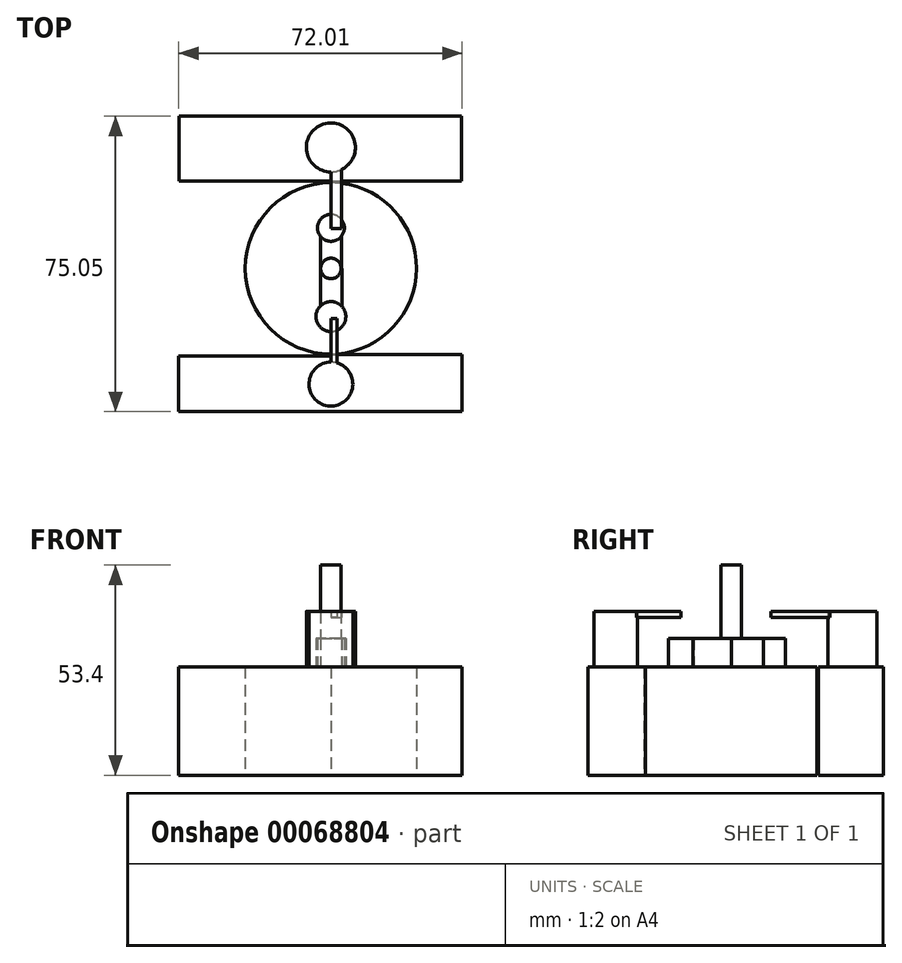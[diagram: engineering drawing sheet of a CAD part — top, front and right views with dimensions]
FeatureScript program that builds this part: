
annotation { "Feature Type Name" : "Feature", "Feature Type Description" : "" }
export const myFeature = defineFeature(function(context is Context, id is Id, definition is map)
    precondition{}
    {
        {
            var Q0;
            Q0=qCreatedBy(makeId("Top.planeOp"),FACE);
            var sketch = newSketch(context, id + "F0", { "sketchPlane" : qUnion([Q0])});
            skCircle(sketch, "E0", {"center": v(0, 0) * mm, "radius": 21.76 * mm});
            skLineSegment(sketch, "E1", {"start": v(0, 0) * mm, "end": v(0, 38.66) * mm});
            skLineSegment(sketch, "E2", {"start": v(0, 38.66) * mm, "end": v(0, 0) * mm});
            skLineSegment(sketch, "E3", {"start": v(0, 0) * mm, "end": v(33.39, 0) * mm});
            skLineSegment(sketch, "E4", {"start": v(33.39, 0) * mm, "end": v(-32.47, 0) * mm});
            skLineSegment(sketch, "E5", {"start": v(-32.47, 0) * mm, "end": v(0, 0) * mm});
            skLineSegment(sketch, "E6", {"start": v(0, -36.39) * mm, "end": v(0, 0) * mm});
            skLineSegment(sketch, "E7.bottom", {"start": v(0, 38.66) * mm, "end": v(-38.56, 38.66) * mm});
            skLineSegment(sketch, "E7.top", {"start": v(0, 22.23) * mm, "end": v(-38.56, 22.23) * mm});
            skLineSegment(sketch, "E7.left", {"start": v(0, 38.66) * mm, "end": v(0, 22.23) * mm});
            skLineSegment(sketch, "E7.right", {"start": v(-38.56, 38.66) * mm, "end": v(-38.56, 22.23) * mm});
            skLineSegment(sketch, "E8.bottom", {"start": v(-38.56, 22.23) * mm, "end": v(-32.47, 22.23) * mm});
            skLineSegment(sketch, "E8.top", {"start": v(-38.56, 0) * mm, "end": v(-32.47, 0) * mm});
            skLineSegment(sketch, "E8.left", {"start": v(-38.56, 22.23) * mm, "end": v(-38.56, 0) * mm});
            skLineSegment(sketch, "E8.right", {"start": v(-32.47, 22.23) * mm, "end": v(-32.47, 0) * mm});
            skLineSegment(sketch, "E9.bottom", {"start": v(0, -36.39) * mm, "end": v(-38.67, -36.39) * mm});
            skLineSegment(sketch, "E9.top", {"start": v(0, -22.24) * mm, "end": v(-38.67, -22.24) * mm});
            skLineSegment(sketch, "E9.left", {"start": v(0, -36.39) * mm, "end": v(0, -22.24) * mm});
            skLineSegment(sketch, "E9.right", {"start": v(-38.67, -36.39) * mm, "end": v(-38.67, -22.24) * mm});
            skLineSegment(sketch, "E10.bottom", {"start": v(-38.56, 0) * mm, "end": v(-32.87, 0) * mm});
            skLineSegment(sketch, "E10.top", {"start": v(-38.56, -22.24) * mm, "end": v(-32.87, -22.24) * mm});
            skLineSegment(sketch, "E10.left", {"start": v(-38.56, 0) * mm, "end": v(-38.56, -22.24) * mm});
            skLineSegment(sketch, "E10.right", {"start": v(-32.87, 0) * mm, "end": v(-32.87, -22.24) * mm});
            skLineSegment(sketch, "E11.bottom", {"start": v(0, 38.66) * mm, "end": v(33.24, 38.66) * mm});
            skLineSegment(sketch, "E11.top", {"start": v(0, 22.13) * mm, "end": v(33.24, 22.13) * mm});
            skLineSegment(sketch, "E11.left", {"start": v(0, 38.66) * mm, "end": v(0, 22.13) * mm});
            skLineSegment(sketch, "E11.right", {"start": v(33.24, 38.66) * mm, "end": v(33.24, 22.13) * mm});
            skLineSegment(sketch, "E12.bottom", {"start": v(33.39, 0) * mm, "end": v(27.74, 0) * mm});
            skLineSegment(sketch, "E12.top", {"start": v(33.39, 22.13) * mm, "end": v(27.74, 22.13) * mm});
            skLineSegment(sketch, "E12.left", {"start": v(33.39, 0) * mm, "end": v(33.39, 22.13) * mm});
            skLineSegment(sketch, "E12.right", {"start": v(27.74, 0) * mm, "end": v(27.74, 22.13) * mm});
            skLineSegment(sketch, "E13.bottom", {"start": v(0, -36.39) * mm, "end": v(33.34, -36.39) * mm});
            skLineSegment(sketch, "E13.top", {"start": v(0, -21.86) * mm, "end": v(33.34, -21.86) * mm});
            skLineSegment(sketch, "E13.left", {"start": v(0, -36.39) * mm, "end": v(0, -21.86) * mm});
            skLineSegment(sketch, "E13.right", {"start": v(33.34, -36.39) * mm, "end": v(33.34, -21.86) * mm});
            skLineSegment(sketch, "E14.bottom", {"start": v(33.34, -21.86) * mm, "end": v(27.74, -21.86) * mm});
            skLineSegment(sketch, "E14.top", {"start": v(33.34, 0) * mm, "end": v(27.74, 0) * mm});
            skLineSegment(sketch, "E14.left", {"start": v(33.34, -21.86) * mm, "end": v(33.34, 0) * mm});
            skLineSegment(sketch, "E14.right", {"start": v(27.74, -21.86) * mm, "end": v(27.74, 0) * mm});
            skSolve(sketch);
        }
        {
            var Q0;
            {var subQ0=sQuery(id+"F0.wireOp",EDGE,"E2");var subQ1=sQuery(id+"F0.wireOp",EDGE,"E0");var subQ2=makeQuery(id+"F0.imprint","INTERSECT",VERTEX,{"derivedFrom":[subQ1,subQ0]});Q0=makeQuery(id+"F0.imprint","IMPRINT",FACE,{"disambiguationData":[TD([[makeQuery(id+"F0.imprint","IMPRINT",EDGE,{"disambiguationData":[TD([[subQ2,-1.0]])],"derivedFrom":subQ1}),1.0]])]});}
            var Q1;
            {var subQ0=sQuery(id+"F0.wireOp",EDGE,"E2");var subQ1=sQuery(id+"F0.wireOp",EDGE,"E0");var subQ2=makeQuery(id+"F0.imprint","INTERSECT",VERTEX,{"derivedFrom":[subQ1,subQ0]});Q1=makeQuery(id+"F0.imprint","IMPRINT",FACE,{"disambiguationData":[TD([[makeQuery(id+"F0.imprint","IMPRINT",EDGE,{"disambiguationData":[TD([[subQ2,1.0]])],"derivedFrom":subQ1}),1.0]])]});}
            var Q2;
            {var subQ0=sQuery(id+"F0.wireOp",EDGE,"E5");var subQ1=sQuery(id+"F0.wireOp",EDGE,"E0");var subQ2=makeQuery(id+"F0.imprint","INTERSECT",VERTEX,{"derivedFrom":[subQ1,subQ0]});Q2=makeQuery(id+"F0.imprint","IMPRINT",FACE,{"disambiguationData":[TD([[makeQuery(id+"F0.imprint","IMPRINT",EDGE,{"disambiguationData":[TD([[subQ2,-1.0]])],"derivedFrom":subQ1}),1.0]])]});}
            var Q3;
            {var subQ0=sQuery(id+"F0.wireOp",EDGE,"E4");var subQ1=sQuery(id+"F0.wireOp",EDGE,"E0");var subQ2=makeQuery(id+"F0.imprint","INTERSECT",VERTEX,{"derivedFrom":[subQ1,subQ0]});Q3=makeQuery(id+"F0.imprint","IMPRINT",FACE,{"disambiguationData":[TD([[makeQuery(id+"F0.imprint","IMPRINT",EDGE,{"disambiguationData":[TD([[subQ2,1.0]])],"derivedFrom":subQ1}),1.0]])]});}
            var Q4;
            Q4=makeQuery(id+"F0.imprint","IMPRINT",FACE,{"disambiguationData":[TD([[makeQuery(id+"F0.imprint","IMPRINT",EDGE,{"derivedFrom":sQuery(id+"F0.wireOp",EDGE,"E12.bottom")}),-1.0]])]});
            var Q5;
            {var subQ3=sQuery(id+"F0.wireOp",EDGE,"E13.bottom");Q5=makeQuery(id+"F0.imprint","IMPRINT",FACE,{"disambiguationData":[TD([[makeQuery(id+"F0.imprint","IMPRINT",EDGE,{"derivedFrom":subQ3}),1.0]])]});}
            var Q6;
            {var subQ5=sQuery(id+"F0.wireOp",EDGE,"E9.bottom");Q6=makeQuery(id+"F0.imprint","IMPRINT",FACE,{"disambiguationData":[TD([[makeQuery(id+"F0.imprint","IMPRINT",EDGE,{"derivedFrom":subQ5}),-1.0]])]});}
            var Q7;
            Q7=makeQuery(id+"F0.imprint","IMPRINT",FACE,{"disambiguationData":[TD([[makeQuery(id+"F0.imprint","IMPRINT",EDGE,{"derivedFrom":sQuery(id+"F0.wireOp",EDGE,"E10.bottom")}),-1.0]])]});
            var Q8;
            Q8=makeQuery(id+"F0.imprint","IMPRINT",FACE,{"disambiguationData":[TD([[makeQuery(id+"F0.imprint","IMPRINT",EDGE,{"derivedFrom":sQuery(id+"F0.wireOp",EDGE,"E8.bottom")}),-1.0]])]});
            var Q9;
            {var subQ1=sQuery(id+"F0.wireOp",EDGE,"E7.bottom");Q9=makeQuery(id+"F0.imprint","IMPRINT",FACE,{"disambiguationData":[TD([[makeQuery(id+"F0.imprint","IMPRINT",EDGE,{"derivedFrom":subQ1}),1.0]])]});}
            var Q10;
            {var subQ3=sQuery(id+"F0.wireOp",EDGE,"E11.bottom");Q10=makeQuery(id+"F0.imprint","IMPRINT",FACE,{"disambiguationData":[TD([[makeQuery(id+"F0.imprint","IMPRINT",EDGE,{"derivedFrom":subQ3}),-1.0]])]});}
            var Q11;
            Q11=makeQuery(id+"F0.imprint","IMPRINT",FACE,{"disambiguationData":[TD([[makeQuery(id+"F0.imprint","IMPRINT",EDGE,{"derivedFrom":sQuery(id+"F0.wireOp",EDGE,"E14.bottom")}),-1.0]])]});
            extrude(context, id + "F1", {"entities" : qUnion([Q0, Q1, Q2, Q3, Q4, Q5, Q6, Q7, Q8, Q9, Q10, Q11]), "depth" : 27.58 * mm});
        }
        {
            var Q0;
            Q0=makeQuery(id+"F1.opExtrude","CAP_FACE",FACE,{"disambiguationData":[OSD([sQuery(id+"F0.wireOp",EDGE,"E0")])],"isStart":false});
            var sketch = newSketch(context, id + "F2", { "sketchPlane" : qUnion([Q0])});
            skCircle(sketch, "E15", {"center": v(0, 10.3) * mm, "radius": 3.41 * mm});
            skCircle(sketch, "E16", {"center": v(0, -12.24) * mm, "radius": 3.8 * mm});
            skSolve(sketch);
        }
        {
            var Q0;
            Q0=makeQuery(id+"F2.imprint","IMPRINT",FACE,{"disambiguationData":[TD([[makeQuery(id+"F2.imprint","IMPRINT",EDGE,{"derivedFrom":sQuery(id+"F2.wireOp",EDGE,"E16")}),1.0]])]});
            var Q1;
            Q1=makeQuery(id+"F2.imprint","IMPRINT",FACE,{"disambiguationData":[TD([[makeQuery(id+"F2.imprint","IMPRINT",EDGE,{"derivedFrom":sQuery(id+"F2.wireOp",EDGE,"E15")}),1.0]])]});
            extrude(context, id + "F3", {"entities" : qUnion([Q0, Q1]), "operationType" : NewBodyOperationType.ADD, "depth" : 7.23 * mm});
        }
        {
            var Q0;
            Q0=makeQuery(id+"F1.opExtrude","CAP_FACE",FACE,{"disambiguationData":[OSD([sQuery(id+"F0.wireOp",EDGE,"E7.bottom"),sQuery(id+"F0.wireOp",EDGE,"E7.top"),sQuery(id+"F0.wireOp",EDGE,"E7.right"),sQuery(id+"F0.wireOp",EDGE,"E8.top"),sQuery(id+"F0.wireOp",EDGE,"E8.left"),sQuery(id+"F0.wireOp",EDGE,"E8.right"),sQuery(id+"F0.wireOp",EDGE,"E9.bottom"),sQuery(id+"F0.wireOp",EDGE,"E9.top"),sQuery(id+"F0.wireOp",EDGE,"E9.right"),sQuery(id+"F0.wireOp",EDGE,"E10.left"),sQuery(id+"F0.wireOp",EDGE,"E10.right"),sQuery(id+"F0.wireOp",EDGE,"E11.bottom"),sQuery(id+"F0.wireOp",EDGE,"E11.top"),sQuery(id+"F0.wireOp",EDGE,"E11.left"),sQuery(id+"F0.wireOp",EDGE,"E11.right"),sQuery(id+"F0.wireOp",EDGE,"E12.bottom"),sQuery(id+"F0.wireOp",EDGE,"E12.top"),sQuery(id+"F0.wireOp",EDGE,"E12.left"),sQuery(id+"F0.wireOp",EDGE,"E12.right"),sQuery(id+"F0.wireOp",EDGE,"E13.bottom"),sQuery(id+"F0.wireOp",EDGE,"E13.top"),sQuery(id+"F0.wireOp",EDGE,"E13.left"),sQuery(id+"F0.wireOp",EDGE,"E13.right"),sQuery(id+"F0.wireOp",EDGE,"E14.left"),sQuery(id+"F0.wireOp",EDGE,"E14.right")])],"isStart":false});
            var sketch = newSketch(context, id + "F4", { "sketchPlane" : qUnion([Q0])});
            skCircle(sketch, "E17", {"center": v(0, 30.74) * mm, "radius": 6.23 * mm});
            skCircle(sketch, "E18", {"center": v(0, -29.4) * mm, "radius": 5.57 * mm});
            skSolve(sketch);
        }
        {
            var Q0;
            Q0=makeQuery(id+"F4.imprint","IMPRINT",FACE,{"disambiguationData":[TD([[makeQuery(id+"F4.imprint","IMPRINT",EDGE,{"derivedFrom":sQuery(id+"F4.wireOp",EDGE,"E18")}),1.0]])]});
            var Q1;
            Q1=makeQuery(id+"F4.imprint","IMPRINT",FACE,{"disambiguationData":[TD([[makeQuery(id+"F4.imprint","IMPRINT",EDGE,{"derivedFrom":sQuery(id+"F4.wireOp",EDGE,"E17")}),1.0]])]});
            extrude(context, id + "F5", {"entities" : qUnion([Q0, Q1]), "operationType" : NewBodyOperationType.ADD, "depth" : 14.06 * mm});
        }
        {
            var Q0;
            Q0=makeQuery(id+"F1.opExtrude","CAP_FACE",FACE,{"disambiguationData":[OSD([sQuery(id+"F0.wireOp",EDGE,"E0")])],"isStart":false});
            var sketch = newSketch(context, id + "F6", { "sketchPlane" : qUnion([Q0])});
            skLineSegment(sketch, "E19.bottom", {"start": v(0, 0) * mm, "end": v(-2.66, 0) * mm});
            skLineSegment(sketch, "E19.top", {"start": v(0, -9.54) * mm, "end": v(-2.66, -9.54) * mm});
            skLineSegment(sketch, "E19.left", {"start": v(0, 0) * mm, "end": v(0, -9.54) * mm});
            skLineSegment(sketch, "E19.right", {"start": v(-2.66, 0) * mm, "end": v(-2.66, -9.54) * mm});
            skLineSegment(sketch, "E20.top", {"start": v(0, 8.15) * mm, "end": v(-2.66, 8.15) * mm});
            skLineSegment(sketch, "E20.left", {"start": v(0, 0) * mm, "end": v(0, 8.15) * mm});
            skLineSegment(sketch, "E20.right", {"start": v(-2.66, 0) * mm, "end": v(-2.66, 8.15) * mm});
            skLineSegment(sketch, "E21.bottom", {"start": v(0, 0) * mm, "end": v(2.68, 0) * mm});
            skLineSegment(sketch, "E21.top", {"start": v(0, 8.18) * mm, "end": v(2.68, 8.18) * mm});
            skLineSegment(sketch, "E21.left", {"start": v(0, 0) * mm, "end": v(0, 8.18) * mm});
            skLineSegment(sketch, "E21.right", {"start": v(2.68, 0) * mm, "end": v(2.68, 8.18) * mm});
            skLineSegment(sketch, "E22.bottom", {"start": v(0, 0) * mm, "end": v(2.88, 0) * mm});
            skLineSegment(sketch, "E22.top", {"start": v(0, -9.77) * mm, "end": v(2.88, -9.77) * mm});
            skLineSegment(sketch, "E22.left", {"start": v(0, 0) * mm, "end": v(0, -9.77) * mm});
            skLineSegment(sketch, "E22.right", {"start": v(2.88, 0) * mm, "end": v(2.88, -9.77) * mm});
            skSolve(sketch);
        }
        {
            var Q0;
            {var subQ0=sQuery(id+"F6.wireOp",EDGE,"E19.right");Q0=makeQuery(id+"F6.imprint","IMPRINT",FACE,{"disambiguationData":[TD([[makeQuery(id+"F6.imprint","IMPRINT",EDGE,{"derivedFrom":subQ0}),1.0]])]});}
            var Q1;
            {var subQ5=sQuery(id+"F6.wireOp",EDGE,"E22.right");Q1=makeQuery(id+"F6.imprint","IMPRINT",FACE,{"disambiguationData":[TD([[makeQuery(id+"F6.imprint","IMPRINT",EDGE,{"derivedFrom":subQ5}),-1.0]])]});}
            var Q2;
            {var subQ5=sQuery(id+"F6.wireOp",EDGE,"E21.right");Q2=makeQuery(id+"F6.imprint","IMPRINT",FACE,{"disambiguationData":[TD([[makeQuery(id+"F6.imprint","IMPRINT",EDGE,{"derivedFrom":subQ5}),1.0]])]});}
            var Q3;
            {var subQ0=sQuery(id+"F6.wireOp",EDGE,"E19.bottom");Q3=makeQuery(id+"F6.imprint","IMPRINT",FACE,{"disambiguationData":[TD([[makeQuery(id+"F6.imprint","IMPRINT",EDGE,{"derivedFrom":subQ0}),-1.0]])]});}
            extrude(context, id + "F7", {"entities" : qUnion([Q0, Q1, Q2, Q3]), "operationType" : NewBodyOperationType.ADD, "depth" : 7.24 * mm});
        }
        {
            var Q0;
            Q0=makeQuery(id+"F5.opExtrude","CAP_FACE",FACE,{"disambiguationData":[OSD([sQuery(id+"F4.wireOp",EDGE,"E17")])],"isStart":false});
            var sketch = newSketch(context, id + "F8", { "sketchPlane" : qUnion([Q0])});
            skLineSegment(sketch, "E23.bottom", {"start": v(0, 30.74) * mm, "end": v(2.67, 30.74) * mm});
            skLineSegment(sketch, "E23.top", {"start": v(0, 10.08) * mm, "end": v(2.67, 10.08) * mm});
            skLineSegment(sketch, "E23.left", {"start": v(0, 30.74) * mm, "end": v(0, 10.08) * mm});
            skLineSegment(sketch, "E23.right", {"start": v(2.67, 30.74) * mm, "end": v(2.67, 10.08) * mm});
            skSolve(sketch);
        }
        {
            var Q0;
            {var subQ0=sQuery(id+"F8.wireOp",EDGE,"E23.top");Q0=makeQuery(id+"F8.imprint","IMPRINT",FACE,{"disambiguationData":[TD([[makeQuery(id+"F8.imprint","IMPRINT",EDGE,{"derivedFrom":subQ0}),1.0]])]});}
            var Q1;
            {var subQ0=sQuery(id+"F8.wireOp",EDGE,"E23.bottom");Q1=makeQuery(id+"F8.imprint","IMPRINT",FACE,{"disambiguationData":[TD([[makeQuery(id+"F8.imprint","IMPRINT",EDGE,{"derivedFrom":subQ0}),-1.0]])]});}
            extrude(context, id + "F9", {"entities" : qUnion([Q0, Q1]), "operationType" : NewBodyOperationType.ADD, "oppositeDirection" : true, "depth" : 1.57 * mm});
        }
        {
            var Q0;
            Q0=makeQuery(id+"F5.opExtrude","CAP_FACE",FACE,{"disambiguationData":[OSD([sQuery(id+"F4.wireOp",EDGE,"E18")])],"isStart":false});
            var sketch = newSketch(context, id + "F10", { "sketchPlane" : qUnion([Q0])});
            skLineSegment(sketch, "E24.bottom", {"start": v(0, -29.4) * mm, "end": v(1.57, -29.4) * mm});
            skLineSegment(sketch, "E24.top", {"start": v(0, -12.76) * mm, "end": v(1.57, -12.76) * mm});
            skLineSegment(sketch, "E24.left", {"start": v(0, -29.4) * mm, "end": v(0, -12.76) * mm});
            skLineSegment(sketch, "E24.right", {"start": v(1.57, -29.4) * mm, "end": v(1.57, -12.76) * mm});
            skSolve(sketch);
        }
        {
            var Q0;
            {var subQ0=sQuery(id+"F10.wireOp",EDGE,"E24.top");Q0=makeQuery(id+"F10.imprint","IMPRINT",FACE,{"disambiguationData":[TD([[makeQuery(id+"F10.imprint","IMPRINT",EDGE,{"derivedFrom":subQ0}),-1.0]])]});}
            var Q1;
            {var subQ0=sQuery(id+"F10.wireOp",EDGE,"E24.bottom");Q1=makeQuery(id+"F10.imprint","IMPRINT",FACE,{"disambiguationData":[TD([[makeQuery(id+"F10.imprint","IMPRINT",EDGE,{"derivedFrom":subQ0}),1.0]])]});}
            extrude(context, id + "F11", {"entities" : qUnion([Q0, Q1]), "operationType" : NewBodyOperationType.ADD, "oppositeDirection" : true, "depth" : 1.6 * mm});
        }
        {
            var Q0;
            Q0=makeQuery(id+"F7.opExtrude","CAP_FACE",FACE,{"disambiguationData":[OSD([sQuery(id+"F2.wireOp",EDGE,"E15"),sQuery(id+"F2.wireOp",EDGE,"E16"),sQuery(id+"F6.wireOp",EDGE,"E19.right"),sQuery(id+"F6.wireOp",EDGE,"E20.right"),sQuery(id+"F6.wireOp",EDGE,"E21.right"),sQuery(id+"F6.wireOp",EDGE,"E22.bottom"),sQuery(id+"F6.wireOp",EDGE,"E22.right")])],"isStart":false});
            var sketch = newSketch(context, id + "F12", { "sketchPlane" : qUnion([Q0])});
            skCircle(sketch, "E25", {"center": v(0, 0) * mm, "radius": 2.6 * mm});
            skSolve(sketch);
        }
        {
            var Q0;
            Q0=makeQuery(id+"F12.imprint","IMPRINT",FACE,{"disambiguationData":[TD([[makeQuery(id+"F12.imprint","IMPRINT",EDGE,{"derivedFrom":sQuery(id+"F12.wireOp",EDGE,"E25")}),1.0]])]});
            extrude(context, id + "F13", {"entities" : qUnion([Q0]), "operationType" : NewBodyOperationType.ADD, "depth" : 18.58 * mm});
        }
    });
